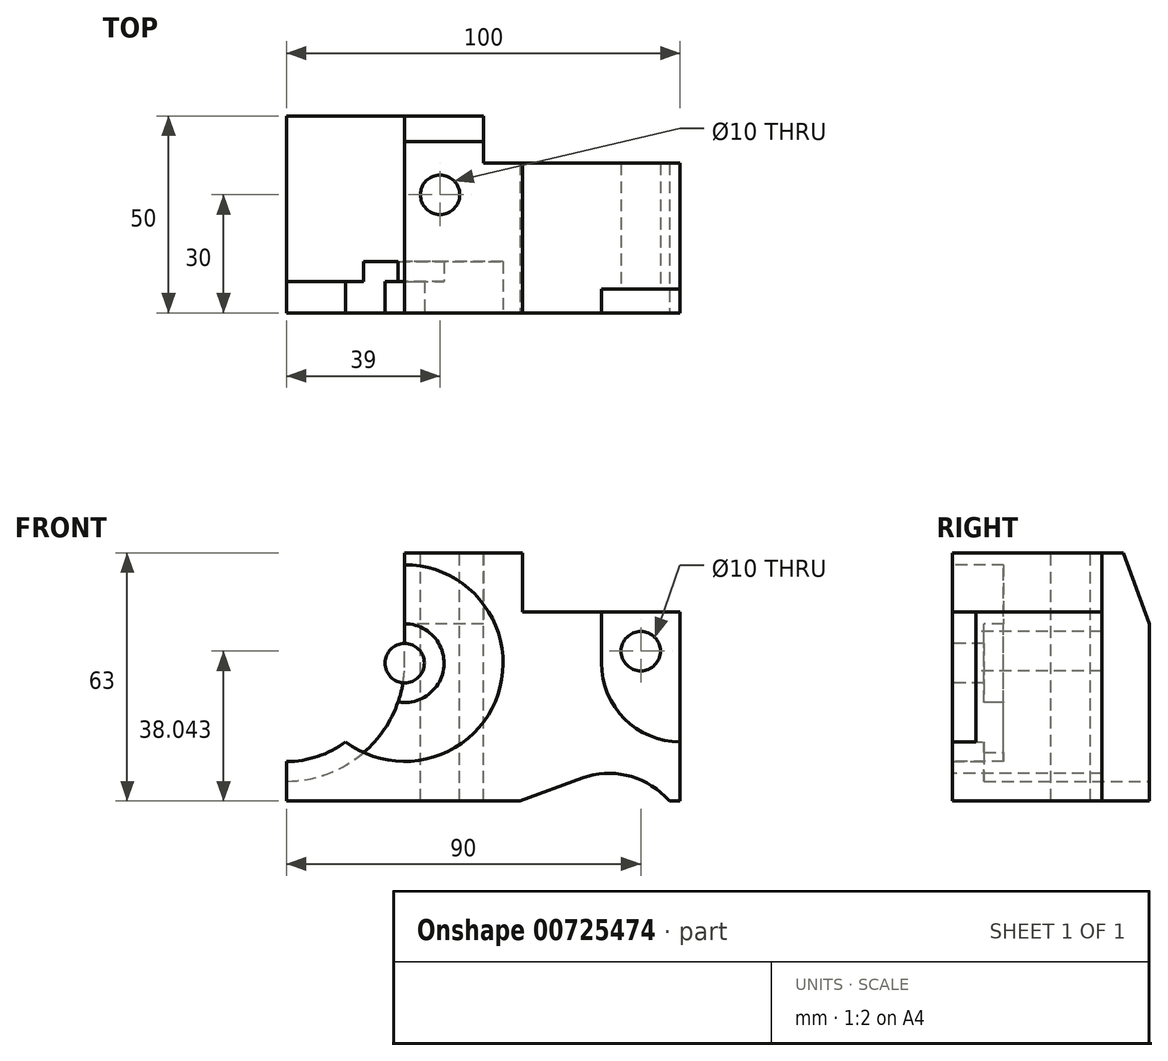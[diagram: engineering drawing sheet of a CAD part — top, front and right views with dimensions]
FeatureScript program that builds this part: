
annotation { "Feature Type Name" : "Feature", "Feature Type Description" : "" }
export const myFeature = defineFeature(function(context is Context, id is Id, definition is map)
    precondition{}
    {
        {
            var Q0;
            Q0=qCreatedBy(makeId("Front.planeOp"),FACE);
            var sketch = newSketch(context, id + "F0", { "sketchPlane" : qUnion([Q0])});
            skLineSegment(sketch, "E0", {"start": v(0, 0) * mm, "end": v(100, 0) * mm});
            skLineSegment(sketch, "E1", {"start": v(100, 0) * mm, "end": v(100, 63) * mm});
            skLineSegment(sketch, "E2", {"start": v(100, 63) * mm, "end": v(0, 63) * mm});
            skLineSegment(sketch, "E3", {"start": v(0, 63) * mm, "end": v(0, 0) * mm});
            skSolve(sketch);
        }
        {
            var Q0;
            Q0 = qSketchRegion(id + "F0", true);
            extrude(context, id + "F1", {"entities" : qUnion([Q0]), "depth" : 50 * mm, "offsetDistance" : 25 * mm});
        }
        {
            var Q0;
            Q0=makeQuery(id+"F1.opExtrude","CAP_FACE",FACE,{"disambiguationData":[OSD([sQuery(id+"F0.wireOp",EDGE,"E0"),sQuery(id+"F0.wireOp",EDGE,"E1"),sQuery(id+"F0.wireOp",EDGE,"E2"),sQuery(id+"F0.wireOp",EDGE,"E3")])],"isStart":false});
            var sketch = newSketch(context, id + "F2", { "sketchPlane" : qUnion([Q0])});
            skLineSegment(sketch, "E4", {"start": v(59.25, 0) * mm, "end": v(75.14, 5.78) * mm});
            skLineSegment(sketch, "E5", {"start": v(96.12, 1.13) * mm, "end": v(97.25, 0) * mm});
            skPoint(sketch, "E6.visualSharp", {"position": v(87.11, 10.14) * mm});
            skArc(sketch, "E6.filletArc", {"start": v(96.12, 1.13) * mm, "mid": v(86.3, 6.52) * mm, "end": v(75.14, 5.78) * mm});
            skCircle(sketch, "E7", {"center": v(30, 35) * mm, "radius": 25 * mm});
            skCircle(sketch, "E8", {"center": v(30, 35) * mm, "radius": 10 * mm});
            skCircle(sketch, "E9", {"center": v(30, 35) * mm, "radius": 5 * mm});
            skLineSegment(sketch, "E10", {"start": v(60, 63) * mm, "end": v(60, 48) * mm});
            skLineSegment(sketch, "E11", {"start": v(60, 48) * mm, "end": v(100, 48) * mm});
            skLineSegment(sketch, "E12", {"start": v(100, 48) * mm, "end": v(100, 63) * mm});
            skLineSegment(sketch, "E13", {"start": v(100, 63) * mm, "end": v(60, 63) * mm});
            skLineSegment(sketch, "E14", {"start": v(80, 48) * mm, "end": v(80, 35) * mm});
            skArc(sketch, "E15", {"start": v(80, 35) * mm, "mid": v(85.86, 20.86) * mm, "end": v(100, 15) * mm});
            skSolve(sketch);
        }
        {
            var Q0;
            {var subQ3=sQuery(id+"F2.wireOp",EDGE,"E14");Q0=makeQuery(id+"F2.imprint","IMPRINT",FACE,{"disambiguationData":[TD([[makeQuery(id+"F2.imprint","IMPRINT",EDGE,{"derivedFrom":subQ3}),1.0]])]});}
            extrude(context, id + "F3", {"entities" : qUnion([Q0]), "operationType" : NewBodyOperationType.REMOVE, "oppositeDirection" : true, "depth" : 6 * mm, "offsetDistance" : 25 * mm});
        }
        {
            var Q0;
            {var subQ3=sQuery(id+"F2.wireOp",EDGE,"E10");Q0=makeQuery(id+"F2.imprint","IMPRINT",FACE,{"disambiguationData":[TD([[makeQuery(id+"F2.imprint","IMPRINT",EDGE,{"derivedFrom":subQ3}),1.0]])]});}
            extrude(context, id + "F4", {"entities" : qUnion([Q0]), "operationType" : NewBodyOperationType.REMOVE, "oppositeDirection" : true, "depth" : 50 * mm, "offsetDistance" : 25 * mm});
        }
        {
            var Q0;
            {var subQ0=sQuery(id+"F2.wireOp",EDGE,"E4");Q0=makeQuery(id+"F2.imprint","IMPRINT",FACE,{"disambiguationData":[TD([[makeQuery(id+"F2.imprint","IMPRINT",EDGE,{"derivedFrom":subQ0}),-1.0]])]});}
            extrude(context, id + "F5", {"entities" : qUnion([Q0]), "operationType" : NewBodyOperationType.REMOVE, "oppositeDirection" : true, "depth" : 50 * mm, "offsetDistance" : 25 * mm});
        }
        {
            var Q0;
            Q0=makeQuery(id+"F2.imprint","IMPRINT",FACE,{"disambiguationData":[TD([[makeQuery(id+"F2.imprint","IMPRINT",EDGE,{"derivedFrom":sQuery(id+"F2.wireOp",EDGE,"E8")}),1.0]])]});
            extrude(context, id + "F6", {"entities" : qUnion([Q0]), "operationType" : NewBodyOperationType.REMOVE, "oppositeDirection" : true, "depth" : 8 * mm, "offsetDistance" : 25 * mm});
        }
        {
            var Q0;
            Q0=makeQuery(id+"F2.imprint","IMPRINT",FACE,{"disambiguationData":[TD([[makeQuery(id+"F2.imprint","IMPRINT",EDGE,{"derivedFrom":sQuery(id+"F2.wireOp",EDGE,"E7")}),1.0]])]});
            extrude(context, id + "F7", {"entities" : qUnion([Q0]), "operationType" : NewBodyOperationType.REMOVE, "oppositeDirection" : true, "depth" : 13 * mm, "offsetDistance" : 25 * mm});
        }
        {
            var Q0;
            Q0=makeQuery(id+"F1.opExtrude","SWEPT_FACE",FACE,{"disambiguationData":[OSD([sQuery(id+"F0.wireOp",EDGE,"E2")])]});
            var sketch = newSketch(context, id + "F8", { "sketchPlane" : qUnion([Q0])});
            skLineSegment(sketch, "E16", {"start": v(60, -12) * mm, "end": v(50, -12) * mm});
            skLineSegment(sketch, "E17", {"start": v(50, -12) * mm, "end": v(50, 0) * mm});
            skLineSegment(sketch, "E18", {"start": v(50, 0) * mm, "end": v(60, 0) * mm});
            skLineSegment(sketch, "E19", {"start": v(60, 0) * mm, "end": v(60, -12) * mm});
            skSolve(sketch);
        }
        {
            var Q0;
            Q0=makeQuery(id+"F8.imprint","IMPRINT",FACE,{"disambiguationData":[TD([[makeQuery(id+"F8.imprint","IMPRINT",EDGE,{"derivedFrom":sQuery(id+"F8.wireOp",EDGE,"E16")}),-1.0]])]});
            extrude(context, id + "F9", {"entities" : qUnion([Q0]), "operationType" : NewBodyOperationType.REMOVE, "oppositeDirection" : true, "depth" : 63 * mm, "offsetDistance" : 25 * mm});
        }
        {
            var Q0;
            Q0=makeQuery(id+"F4.boolean.opBoolean","COPY",FACE,{"derivedFrom":makeQuery(id+"F4.opExtrude","SWEPT_FACE",FACE,{"disambiguationData":[OSD([sQuery(id+"F2.wireOp",EDGE,"E11")])]})});
            var sketch = newSketch(context, id + "F10", { "sketchPlane" : qUnion([Q0])});
            skLineSegment(sketch, "E20", {"start": v(60, -12) * mm, "end": v(100, -12) * mm});
            skLineSegment(sketch, "E21", {"start": v(100, -12) * mm, "end": v(100, 0) * mm});
            skLineSegment(sketch, "E22", {"start": v(100, 0) * mm, "end": v(60, 0) * mm});
            skLineSegment(sketch, "E23", {"start": v(60, 0) * mm, "end": v(60, -12) * mm});
            skSolve(sketch);
        }
        {
            var Q0;
            Q0=makeQuery(id+"F10.imprint","IMPRINT",FACE,{"disambiguationData":[TD([[makeQuery(id+"F10.imprint","IMPRINT",EDGE,{"derivedFrom":sQuery(id+"F10.wireOp",EDGE,"E20")}),1.0]])]});
            extrude(context, id + "F11", {"entities" : qUnion([Q0]), "operationType" : NewBodyOperationType.REMOVE, "oppositeDirection" : true, "depth" : 63 * mm, "offsetDistance" : 25 * mm});
        }
        {
            var Q0;
            Q0=makeQuery(id+"F3.boolean.opBoolean","COPY",FACE,{"derivedFrom":makeQuery(id+"F3.opExtrude","CAP_FACE",FACE,{"disambiguationData":[OSD([sQuery(id+"F0.wireOp",EDGE,"E1"),sQuery(id+"F2.wireOp",EDGE,"E11"),sQuery(id+"F2.wireOp",EDGE,"E14"),sQuery(id+"F2.wireOp",EDGE,"E15")])],"isStart":false})});
            var sketch = newSketch(context, id + "F12", { "sketchPlane" : qUnion([Q0])});
            skCircle(sketch, "E24", {"center": v(90, 38.04) * mm, "radius": 5 * mm});
            skPoint(sketch, "E24.centerSnap0", {"position": v(90, 48) * mm});
            skSolve(sketch);
        }
        {
            var Q0;
            Q0=makeQuery(id+"F12.imprint","IMPRINT",FACE,{"disambiguationData":[TD([[makeQuery(id+"F12.imprint","IMPRINT",EDGE,{"derivedFrom":sQuery(id+"F12.wireOp",EDGE,"E24")}),1.0]])]});
            extrude(context, id + "F13", {"entities" : qUnion([Q0]), "operationType" : NewBodyOperationType.REMOVE, "oppositeDirection" : true, "depth" : 50 * mm, "offsetDistance" : 25 * mm});
        }
        {
            var Q0;
            {var subQ0=sQuery(id+"F0.wireOp",EDGE,"E0");var subQ1=sQuery(id+"F0.wireOp",EDGE,"E3");var subQ2=sQuery(id+"F0.wireOp",EDGE,"E2");Q0=makeQuery(id+"F9.boolean.opBoolean","SPLIT",FACE,{"disambiguationData":[TD([makeQuery(id+"F1.opExtrude","SWEPT_FACE",FACE,{"disambiguationData":[OSD([subQ2])]})])],"derivedFrom":makeQuery(id+"F1.opExtrude","CAP_FACE",FACE,{"disambiguationData":[OSD([subQ0,sQuery(id+"F0.wireOp",EDGE,"E1"),subQ2,subQ1])],"isStart":true})});}
            var sketch = newSketch(context, id + "F14", { "sketchPlane" : qUnion([Q0])});
            skCircle(sketch, "E25", {"center": v(0, 35) * mm, "radius": 25 * mm});
            skCircle(sketch, "E26", {"center": v(0, 35) * mm, "radius": 30 * mm});
            skLineSegment(sketch, "E27", {"start": v(-30, 35) * mm, "end": v(-30, 63) * mm});
            skSolve(sketch);
        }
        {
            var Q0;
            {var subQ0=sQuery(id+"F14.wireOp",EDGE,"E25");var subQ1=makeQuery(id+"F1.opExtrude","CAP_EDGE",EDGE,{"disambiguationData":[OSD([sQuery(id+"F0.wireOp",EDGE,"E3")])],"isStart":true});var subQ2=makeQuery(id+"F14.imprint","INTERSECT",VERTEX,{"disambiguationData":[OD(0.0)],"derivedFrom":[subQ1,subQ0]});Q0=makeQuery(id+"F14.imprint","IMPRINT",FACE,{"disambiguationData":[TD([[makeQuery(id+"F14.imprint","IMPRINT",EDGE,{"disambiguationData":[TD([[subQ2,-1.0]])],"derivedFrom":subQ0}),1.0]])]});}
            var Q1;
            {var subQ0=sQuery(id+"F14.wireOp",EDGE,"E25");var subQ1=makeQuery(id+"F1.opExtrude","CAP_EDGE",EDGE,{"disambiguationData":[OSD([sQuery(id+"F0.wireOp",EDGE,"E3")])],"isStart":true});var subQ2=makeQuery(id+"F14.imprint","INTERSECT",VERTEX,{"disambiguationData":[OD(0.0)],"derivedFrom":[subQ1,subQ0]});Q1=makeQuery(id+"F14.imprint","IMPRINT",FACE,{"disambiguationData":[TD([[makeQuery(id+"F14.imprint","IMPRINT",EDGE,{"disambiguationData":[TD([[subQ2,1.0]])],"derivedFrom":subQ0}),1.0]])]});}
            extrude(context, id + "F15", {"entities" : qUnion([Q0, Q1]), "operationType" : NewBodyOperationType.REMOVE, "oppositeDirection" : true, "depth" : 50 * mm, "offsetDistance" : 25 * mm});
        }
        {
            var Q0;
            {var subQ1=makeQuery(id+"F1.opExtrude","CAP_EDGE",EDGE,{"disambiguationData":[OSD([sQuery(id+"F0.wireOp",EDGE,"E3")])],"isStart":true});var subQ3=sQuery(id+"F14.wireOp",EDGE,"E25");var subQ4=makeQuery(id+"F14.imprint","INTERSECT",VERTEX,{"disambiguationData":[OD(0.0)],"derivedFrom":[subQ1,subQ3]});Q0=makeQuery(id+"F14.imprint","IMPRINT",FACE,{"disambiguationData":[TD([[makeQuery(id+"F14.imprint","IMPRINT",EDGE,{"disambiguationData":[TD([[subQ4,-1.0]])],"derivedFrom":subQ3}),-1.0]])]});}
            var Q1;
            {var subQ1=makeQuery(id+"F1.opExtrude","CAP_EDGE",EDGE,{"disambiguationData":[OSD([sQuery(id+"F0.wireOp",EDGE,"E3")])],"isStart":true});var subQ5=sQuery(id+"F14.wireOp",EDGE,"E25");var subQ6=makeQuery(id+"F14.imprint","INTERSECT",VERTEX,{"disambiguationData":[OD(0.0)],"derivedFrom":[subQ1,subQ5]});Q1=makeQuery(id+"F14.imprint","IMPRINT",FACE,{"disambiguationData":[TD([[makeQuery(id+"F14.imprint","IMPRINT",EDGE,{"disambiguationData":[TD([[subQ6,1.0]])],"derivedFrom":subQ5}),-1.0]])]});}
            extrude(context, id + "F16", {"entities" : qUnion([Q0, Q1]), "operationType" : NewBodyOperationType.REMOVE, "depth" : 42 * mm, "offsetDistance" : 25 * mm});
        }
        {
            var Q0;
            {var subQ1=makeQuery(id+"F1.opExtrude","CAP_EDGE",EDGE,{"disambiguationData":[OSD([sQuery(id+"F0.wireOp",EDGE,"E3")])],"isStart":true});var subQ3=sQuery(id+"F14.wireOp",EDGE,"E25");var subQ4=makeQuery(id+"F14.imprint","INTERSECT",VERTEX,{"disambiguationData":[OD(0.0)],"derivedFrom":[subQ1,subQ3]});Q0=makeQuery(id+"F14.imprint","IMPRINT",FACE,{"disambiguationData":[TD([[makeQuery(id+"F14.imprint","IMPRINT",EDGE,{"disambiguationData":[TD([[subQ4,-1.0]])],"derivedFrom":subQ3}),-1.0]])]});}
            var Q1;
            {var subQ1=makeQuery(id+"F1.opExtrude","CAP_EDGE",EDGE,{"disambiguationData":[OSD([sQuery(id+"F0.wireOp",EDGE,"E3")])],"isStart":true});var subQ5=sQuery(id+"F14.wireOp",EDGE,"E25");var subQ6=makeQuery(id+"F14.imprint","INTERSECT",VERTEX,{"disambiguationData":[OD(0.0)],"derivedFrom":[subQ1,subQ5]});Q1=makeQuery(id+"F14.imprint","IMPRINT",FACE,{"disambiguationData":[TD([[makeQuery(id+"F14.imprint","IMPRINT",EDGE,{"disambiguationData":[TD([[subQ6,1.0]])],"derivedFrom":subQ5}),-1.0]])]});}
            var Q2;
            {var subQ0=sQuery(id+"F14.wireOp",EDGE,"E27");Q2=makeQuery(id+"F14.imprint","IMPRINT",FACE,{"disambiguationData":[TD([[makeQuery(id+"F14.imprint","IMPRINT",EDGE,{"derivedFrom":subQ0}),-1.0]])]});}
            extrude(context, id + "F17", {"entities" : qUnion([Q0, Q1, Q2]), "operationType" : NewBodyOperationType.REMOVE, "oppositeDirection" : true, "depth" : 42 * mm, "offsetDistance" : 25 * mm});
        }
        {
            var Q0;
            Q0=makeQuery(id+"F1.opExtrude","SWEPT_FACE",FACE,{"disambiguationData":[OSD([sQuery(id+"F0.wireOp",EDGE,"E2")])]});
            var sketch = newSketch(context, id + "F18", { "sketchPlane" : qUnion([Q0])});
            skLineSegment(sketch, "E28", {"start": v(30, -42) * mm, "end": v(30, -50) * mm});
            skLineSegment(sketch, "E29", {"start": v(30, -50) * mm, "end": v(0, -50) * mm});
            skLineSegment(sketch, "E30", {"start": v(0, -50) * mm, "end": v(0, -42) * mm});
            skLineSegment(sketch, "E31", {"start": v(0, -42) * mm, "end": v(30, -42) * mm});
            skSolve(sketch);
        }
        {
            var Q0;
            Q0 = qSketchRegion(id + "F18", true);
            extrude(context, id + "F19", {"entities" : qUnion([Q0]), "operationType" : NewBodyOperationType.REMOVE, "oppositeDirection" : true, "depth" : 11.4 * mm, "offsetDistance" : 25 * mm});
        }
        {
            var Q0;
            Q0=makeQuery(id+"F19.boolean.opBoolean","MERGE",FACE,{"derivedFrom":[makeQuery(id+"F17.boolean.opBoolean","COPY",FACE,{"derivedFrom":makeQuery(id+"F17.opExtrude","SWEPT_FACE",FACE,{"disambiguationData":[OSD([sQuery(id+"F14.wireOp",EDGE,"E27")])]})}),makeQuery(id+"F19.opExtrude","SWEPT_FACE",FACE,{"disambiguationData":[OSD([sQuery(id+"F18.wireOp",EDGE,"E28")])]})]});
            var sketch = newSketch(context, id + "F20", { "sketchPlane" : qUnion([Q0])});
            skLineSegment(sketch, "E32", {"start": v(0, 63) * mm, "end": v(0, 45) * mm});
            skLineSegment(sketch, "E33", {"start": v(0, 45) * mm, "end": v(6.55, 63) * mm});
            skLineSegment(sketch, "E34", {"start": v(6.55, 63) * mm, "end": v(0, 63) * mm});
            skSolve(sketch);
        }
        {
            var Q0;
            Q0=makeQuery(id+"F20.imprint","IMPRINT",FACE,{"disambiguationData":[TD([[makeQuery(id+"F20.imprint","IMPRINT",EDGE,{"derivedFrom":sQuery(id+"F20.wireOp",EDGE,"E32")}),-1.0]])]});
            extrude(context, id + "F21", {"entities" : qUnion([Q0]), "operationType" : NewBodyOperationType.REMOVE, "oppositeDirection" : true, "depth" : 100 * mm, "offsetDistance" : 25 * mm});
        }
        {
            var Q0;
            Q0=makeQuery(id+"F1.opExtrude","SWEPT_FACE",FACE,{"disambiguationData":[OSD([sQuery(id+"F0.wireOp",EDGE,"E2")])]});
            var sketch = newSketch(context, id + "F22", { "sketchPlane" : qUnion([Q0])});
            skCircle(sketch, "E35", {"center": v(39, -20) * mm, "radius": 5 * mm});
            skSolve(sketch);
        }
        {
            var Q0;
            Q0=makeQuery(id+"F22.imprint","IMPRINT",FACE,{"disambiguationData":[TD([[makeQuery(id+"F22.imprint","IMPRINT",EDGE,{"derivedFrom":sQuery(id+"F22.wireOp",EDGE,"E35")}),1.0]])]});
            extrude(context, id + "F23", {"entities" : qUnion([Q0]), "operationType" : NewBodyOperationType.REMOVE, "oppositeDirection" : true, "depth" : 63 * mm, "offsetDistance" : 25 * mm});
        }
    });
